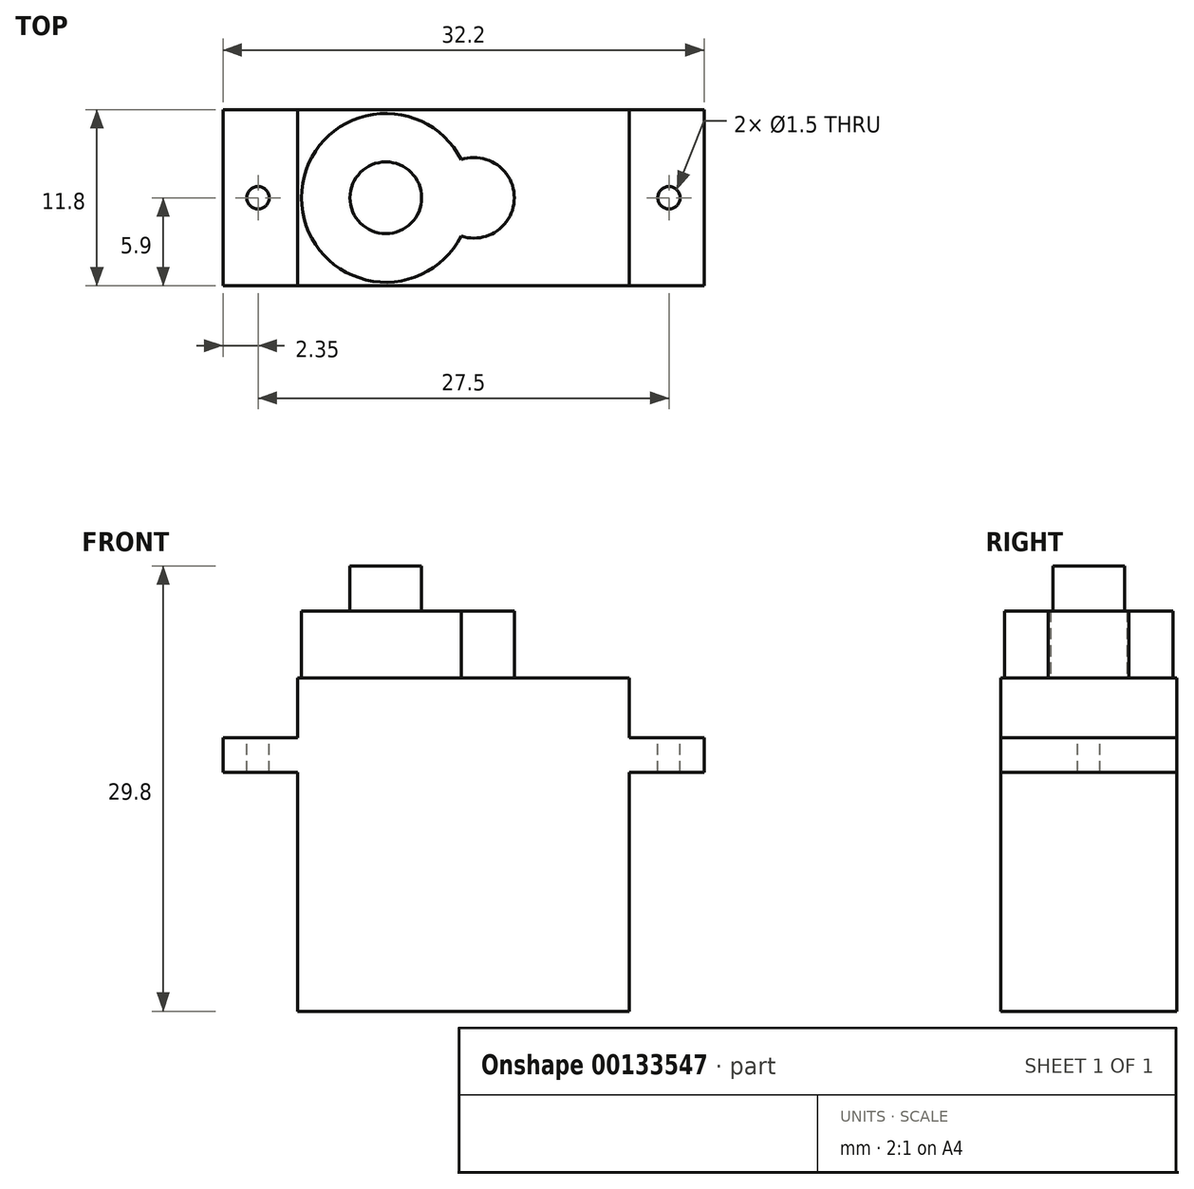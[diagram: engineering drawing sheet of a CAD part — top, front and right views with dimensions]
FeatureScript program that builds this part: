
annotation { "Feature Type Name" : "Feature", "Feature Type Description" : "" }
export const myFeature = defineFeature(function(context is Context, id is Id, definition is map)
    precondition{}
    {
        {
            var Q0;
            Q0=qCreatedBy(makeId("Front.planeOp"),FACE);
            var sketch = newSketch(context, id + "F0", { "sketchPlane" : qUnion([Q0])});
            skLineSegment(sketch, "E0", {"start": v(0, 0) * mm, "end": v(0, 22.3) * mm, "construction": true});
            skLineSegment(sketch, "E1", {"start": v(0, 22.3) * mm, "end": v(32.2, 22.3) * mm, "construction": true});
            skLineSegment(sketch, "E2", {"start": v(32.2, 22.3) * mm, "end": v(32.2, 0) * mm, "construction": true});
            skLineSegment(sketch, "E3", {"start": v(32.2, 0) * mm, "end": v(0, 0) * mm, "construction": true});
            skLineSegment(sketch, "E4", {"start": v(0, 16) * mm, "end": v(32.2, 16) * mm, "construction": true});
            skLineSegment(sketch, "E5", {"start": v(0, 18.3) * mm, "end": v(32.2, 18.3) * mm, "construction": true});
            skLineSegment(sketch, "E6", {"start": v(5, 22.3) * mm, "end": v(5, 0) * mm, "construction": true});
            skLineSegment(sketch, "E7", {"start": v(27.2, 22.3) * mm, "end": v(27.2, 0) * mm, "construction": true});
            skLineSegment(sketch, "E8", {"start": v(5, 0) * mm, "end": v(5, 16) * mm});
            skLineSegment(sketch, "E9", {"start": v(5, 16) * mm, "end": v(0, 16) * mm});
            skLineSegment(sketch, "E10", {"start": v(0, 18.3) * mm, "end": v(5, 18.3) * mm});
            skLineSegment(sketch, "E11", {"start": v(5, 18.3) * mm, "end": v(5, 22.3) * mm});
            skLineSegment(sketch, "E12", {"start": v(27.2, 22.3) * mm, "end": v(27.2, 18.3) * mm});
            skLineSegment(sketch, "E13", {"start": v(27.2, 18.3) * mm, "end": v(32.2, 18.3) * mm});
            skLineSegment(sketch, "E14", {"start": v(32.2, 16) * mm, "end": v(27.2, 16) * mm});
            skLineSegment(sketch, "E15", {"start": v(27.2, 16) * mm, "end": v(27.2, 0) * mm});
            skLineSegment(sketch, "E16", {"start": v(5, 0) * mm, "end": v(27.2, 0) * mm});
            skLineSegment(sketch, "E17", {"start": v(5, 22.3) * mm, "end": v(27.2, 22.3) * mm});
            skLineSegment(sketch, "E18", {"start": v(0, 18.3) * mm, "end": v(0, 16) * mm});
            skLineSegment(sketch, "E19", {"start": v(32.2, 18.3) * mm, "end": v(32.2, 16) * mm});
            skSolve(sketch);
        }
        {
            var Q0;
            Q0 = qSketchRegion(id + "F0", true);
            extrude(context, id + "F1", {"entities" : qUnion([Q0]), "depth" : 11.8 * mm});
        }
        {
            var Q0;
            Q0=makeQuery(id+"F1.opExtrude","SWEPT_FACE",FACE,{"disambiguationData":[OSD([sQuery(id+"F0.wireOp",EDGE,"E17")])]});
            var sketch = newSketch(context, id + "F2", { "sketchPlane" : qUnion([Q0])});
            skCircle(sketch, "E20", {"center": v(10.9, -5.9) * mm, "radius": 5.65 * mm});
            skCircle(sketch, "E21", {"center": v(16.8, -5.9) * mm, "radius": 2.7 * mm});
            skLineSegment(sketch, "E22", {"start": v(5, -5.9) * mm, "end": v(27.2, -5.9) * mm, "construction": true});
            skLineSegment(sketch, "E23", {"start": v(16.8, -3.2) * mm, "end": v(15.86, -3.2) * mm});
            skLineSegment(sketch, "E24", {"start": v(16.8, -8.6) * mm, "end": v(15.86, -8.6) * mm});
            skLineSegment(sketch, "E25", {"start": v(16.8, -5.9) * mm, "end": v(16.8, -11.8) * mm, "construction": true});
            skLineSegment(sketch, "E26", {"start": v(16.8, -5.9) * mm, "end": v(16.8, 0) * mm, "construction": true});
            skCircle(sketch, "E27", {"center": v(10.9, -5.9) * mm, "radius": 2.4 * mm});
            skLineSegment(sketch, "E28", {"start": v(0, -5.9) * mm, "end": v(5, -5.9) * mm, "construction": true});
            skLineSegment(sketch, "E29", {"start": v(27.2, -5.9) * mm, "end": v(32.2, -5.9) * mm, "construction": true});
            skCircle(sketch, "E30", {"center": v(2.35, -5.9) * mm, "radius": 0.75 * mm});
            skCircle(sketch, "E31", {"center": v(29.85, -5.9) * mm, "radius": 0.75 * mm});
            skLineSegment(sketch, "E32", {"start": v(2.35, -5.9) * mm, "end": v(0, -5.9) * mm, "construction": true});
            skLineSegment(sketch, "E33", {"start": v(32.2, -5.9) * mm, "end": v(29.85, -5.9) * mm, "construction": true});
            skSolve(sketch);
        }
        {
            var Q0;
            {var subQ0=sQuery(id+"F2.wireOp",EDGE,"E21");var subQ1=sQuery(id+"F2.wireOp",EDGE,"E20");var subQ2=makeQuery(id+"F2.imprint","INTERSECT",VERTEX,{"disambiguationData":[OD(0.0)],"derivedFrom":[subQ1,subQ0]});Q0=makeQuery(id+"F2.imprint","IMPRINT",FACE,{"disambiguationData":[TD([[makeQuery(id+"F2.imprint","IMPRINT",EDGE,{"disambiguationData":[TD([[subQ2,1.0]])],"derivedFrom":subQ1}),1.0]])]});}
            var Q1;
            Q1=makeQuery(id+"F2.imprint","IMPRINT",FACE,{"disambiguationData":[TD([[makeQuery(id+"F2.imprint","IMPRINT",EDGE,{"derivedFrom":sQuery(id+"F2.wireOp",EDGE,"E27")}),-1.0]])]});
            var Q2;
            {var subQ0=sQuery(id+"F2.wireOp",EDGE,"E21");var subQ1=sQuery(id+"F2.wireOp",EDGE,"E20");var subQ2=makeQuery(id+"F2.imprint","INTERSECT",VERTEX,{"disambiguationData":[OD(0.0)],"derivedFrom":[subQ1,subQ0]});Q2=makeQuery(id+"F2.imprint","IMPRINT",FACE,{"disambiguationData":[TD([[makeQuery(id+"F2.imprint","IMPRINT",EDGE,{"disambiguationData":[TD([[subQ2,1.0]])],"derivedFrom":subQ1}),-1.0]])]});}
            extrude(context, id + "F3", {"entities" : qUnion([Q0, Q1, Q2]), "operationType" : NewBodyOperationType.ADD, "depth" : 4.5 * mm});
        }
        {
            var Q0;
            Q0=makeQuery(id+"F3.boolean.opBoolean","SPLIT",FACE,{"disambiguationData":[TD([makeQuery(id+"F3.opExtrude","SWEPT_FACE",FACE,{"disambiguationData":[OSD([sQuery(id+"F2.wireOp",EDGE,"E27")])]})])],"derivedFrom":makeQuery(id+"F1.opExtrude","SWEPT_FACE",FACE,{"disambiguationData":[OSD([sQuery(id+"F0.wireOp",EDGE,"E17")])]})});
            extrude(context, id + "F4", {"entities" : qUnion([Q0]), "operationType" : NewBodyOperationType.ADD, "depth" : 7.5 * mm});
        }
        {
            var Q0;
            Q0=makeQuery(id+"F2.imprint","IMPRINT",FACE,{"disambiguationData":[TD([[makeQuery(id+"F2.imprint","IMPRINT",EDGE,{"derivedFrom":sQuery(id+"F2.wireOp",EDGE,"E30")}),1.0]])]});
            var Q1;
            Q1=makeQuery(id+"F2.imprint","IMPRINT",FACE,{"disambiguationData":[TD([[makeQuery(id+"F2.imprint","IMPRINT",EDGE,{"derivedFrom":sQuery(id+"F2.wireOp",EDGE,"E31")}),1.0]])]});
            extrude(context, id + "F5", {"entities" : qUnion([Q0, Q1]), "operationType" : NewBodyOperationType.REMOVE, "endBound" : BoundingType.THROUGH_ALL, "oppositeDirection" : true, "depth" : 25 * mm});
        }
    });
